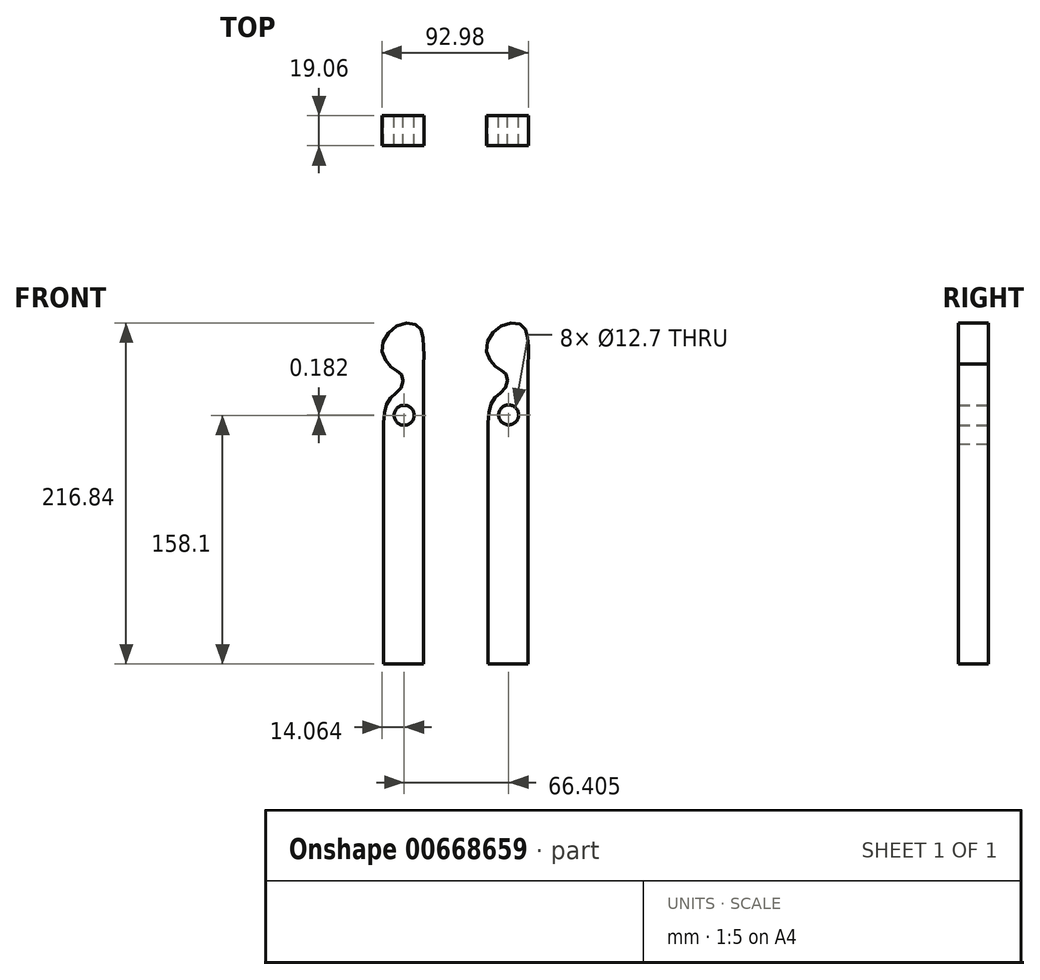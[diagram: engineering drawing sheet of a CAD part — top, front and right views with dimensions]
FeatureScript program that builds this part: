
annotation { "Feature Type Name" : "Feature", "Feature Type Description" : "" }
export const myFeature = defineFeature(function(context is Context, id is Id, definition is map)
    precondition{}
    {
        {
            var Q0;
            Q0=qCreatedBy(makeId("Front.planeOp"),FACE);
            var sketch = newSketch(context, id + "F0", { "sketchPlane" : qUnion([Q0])});
            skLineSegment(sketch, "E0", {"start": v(-57.26, -106.86) * mm, "end": v(-31.86, -106.86) * mm});
            skLineSegment(sketch, "E1", {"start": v(-31.86, -106.86) * mm, "end": v(-31.86, 83.64) * mm});
            skLineSegment(sketch, "E2", {"start": v(-57.26, -106.86) * mm, "end": v(-57.26, 32.84) * mm});
            skFitSpline(sketch, "E3", {"points": [v(-31.86, 83.64) * mm, v(-31.86, 97.05) * mm, v(-35.68, 108.2) * mm, v(-50.24, 107.18) * mm, v(-58.24, 92.2) * mm, v(-51.48, 81.13) * mm, v(-45.94, 77.03) * mm, v(-45.94, 69.03) * mm, v(-52.7, 62.49) * mm, v(-56.75, 52.33) * mm, v(-57.26, 32.84) * mm], "startDerivative": vector(3.65, 130.6) * mm, "endDerivative": vector(2.66, -130.68) * mm});
            skCircle(sketch, "E4", {"center": v(-44.23, 51.24) * mm, "radius": 6.35 * mm});
            skLineSegment(sketch, "E5", {"start": v(9.14, -106.67) * mm, "end": v(34.54, -106.67) * mm});
            skLineSegment(sketch, "E6", {"start": v(34.54, -106.67) * mm, "end": v(34.54, 83.83) * mm});
            skLineSegment(sketch, "E7", {"start": v(9.14, -106.67) * mm, "end": v(9.14, 33.03) * mm});
            skFitSpline(sketch, "E8", {"points": [v(34.54, 83.83) * mm, v(34.54, 97.24) * mm, v(30.72, 108.39) * mm, v(16.16, 107.36) * mm, v(8.16, 92.39) * mm, v(14.93, 81.31) * mm, v(20.47, 77.21) * mm, v(20.47, 69.22) * mm, v(13.71, 62.67) * mm, v(9.66, 52.5) * mm, v(9.14, 33.03) * mm], "startDerivative": vector(3.65, 130.6) * mm, "endDerivative": vector(2.66, -130.68) * mm});
            skCircle(sketch, "E9", {"center": v(22.18, 51.42) * mm, "radius": 6.35 * mm});
            skSolve(sketch);
        }
        {
            var Q0;
            Q0 = qSketchRegion(id + "F0", true);
            extrude(context, id + "F1", {"entities" : qUnion([Q0]), "endBound" : BoundingType.SYMMETRIC, "depth" : 19.05 * mm, "offsetDistance" : 25.4 * mm});
        }
    });
